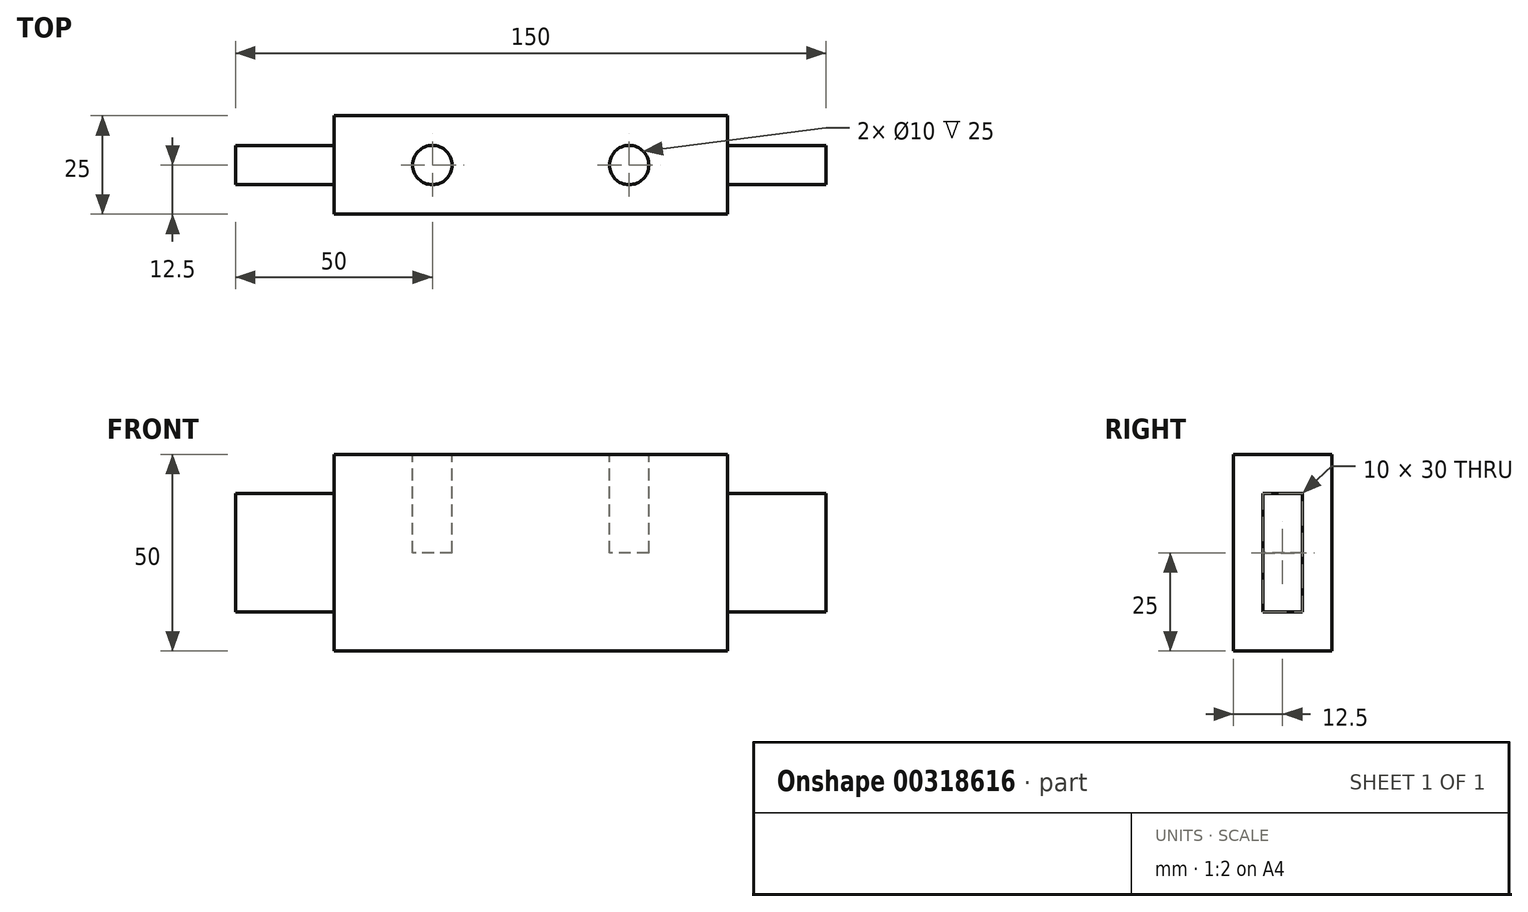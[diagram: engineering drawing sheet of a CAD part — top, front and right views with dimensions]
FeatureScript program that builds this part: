
annotation { "Feature Type Name" : "Feature", "Feature Type Description" : "" }
export const myFeature = defineFeature(function(context is Context, id is Id, definition is map)
    precondition{}
    {
        {
            var Q0;
            Q0=qCreatedBy(makeId("Right.planeOp"),FACE);
            var sketch = newSketch(context, id + "F0", { "sketchPlane" : qUnion([Q0])});
            skLineSegment(sketch, "E0.rect.bottom", {"start": v(12.5, -25) * mm, "end": v(-12.5, -25) * mm});
            skLineSegment(sketch, "E0.rect.top", {"start": v(12.5, 25) * mm, "end": v(-12.5, 25) * mm});
            skLineSegment(sketch, "E0.rect.left", {"start": v(12.5, -25) * mm, "end": v(12.5, 25) * mm});
            skLineSegment(sketch, "E0.rect.right", {"start": v(-12.5, -25) * mm, "end": v(-12.5, 25) * mm});
            skPoint(sketch, "E0.rect.middle", {"position": v(0, 0) * mm});
            skSolve(sketch);
        }
        {
            var Q0;
            Q0=makeQuery(id+"F0.imprint","IMPRINT",FACE,{"disambiguationData":[TD([[makeQuery(id+"F0.imprint","IMPRINT",EDGE,{"derivedFrom":sQuery(id+"F0.wireOp",EDGE,"E0.rect.bottom")}),-1.0]])]});
            extrude(context, id + "F1", {"entities" : qUnion([Q0]), "endBound" : BoundingType.SYMMETRIC, "depth" : 100 * mm});
        }
        {
            var Q0;
            Q0=makeQuery(id+"F1.opExtrude","CAP_FACE",FACE,{"disambiguationData":[OSD([sQuery(id+"F0.wireOp",EDGE,"E0.rect.bottom"),sQuery(id+"F0.wireOp",EDGE,"E0.rect.top"),sQuery(id+"F0.wireOp",EDGE,"E0.rect.left"),sQuery(id+"F0.wireOp",EDGE,"E0.rect.right")])],"isStart":false});
            var sketch = newSketch(context, id + "F2", { "sketchPlane" : qUnion([Q0])});
            skLineSegment(sketch, "E1.rect.bottom", {"start": v(5, -15) * mm, "end": v(-5, -15) * mm});
            skLineSegment(sketch, "E1.rect.top", {"start": v(5, 15) * mm, "end": v(-5, 15) * mm});
            skLineSegment(sketch, "E1.rect.left", {"start": v(5, -15) * mm, "end": v(5, 15) * mm});
            skLineSegment(sketch, "E1.rect.right", {"start": v(-5, -15) * mm, "end": v(-5, 15) * mm});
            skPoint(sketch, "E1.rect.middle", {"position": v(0, 0) * mm});
            skSolve(sketch);
        }
        {
            var Q0;
            Q0=qSketchRegion(id+"F2",true);
            extrude(context, id + "F3", {"entities" : qUnion([Q0]), "operationType" : NewBodyOperationType.ADD, "depth" : 25 * mm});
        }
        {
            var Q0;
            Q0=makeQuery(id+"F1.opExtrude","SWEPT_BODY",BODY,{"disambiguationData":[OSD([sQuery(id+"F0.wireOp",EDGE,"E0.rect.bottom"),sQuery(id+"F0.wireOp",EDGE,"E0.rect.top"),sQuery(id+"F0.wireOp",EDGE,"E0.rect.left"),sQuery(id+"F0.wireOp",EDGE,"E0.rect.right")])]});
            var Q1;
            Q1=qCreatedBy(makeId("Right.planeOp"),FACE);
            mirror(context, id + "F4", {"operationType" : NewBodyOperationType.ADD, "entities" : qUnion([Q0]), "mirrorPlane" : qUnion([Q1])});
        }
        {
            var Q0;
            Q0=makeQuery(id+"F1.opExtrude","SWEPT_FACE",FACE,{"disambiguationData":[OSD([sQuery(id+"F0.wireOp",EDGE,"E0.rect.top")])]});
            var sketch = newSketch(context, id + "F5", { "sketchPlane" : qUnion([Q0])});
            skLineSegment(sketch, "E2", {"start": v(-50, 0) * mm, "end": v(50, 0) * mm, "construction": true});
            skCircle(sketch, "E3", {"center": v(-25, 0) * mm, "radius": 5 * mm});
            skCircle(sketch, "E4", {"center": v(25, 0) * mm, "radius": 5 * mm});
            skSolve(sketch);
        }
        {
            var Q0;
            Q0=qSketchRegion(id+"F5",true);
            extrude(context, id + "F6", {"entities" : qUnion([Q0]), "operationType" : NewBodyOperationType.REMOVE, "oppositeDirection" : true, "depth" : 25 * mm});
        }
    });
